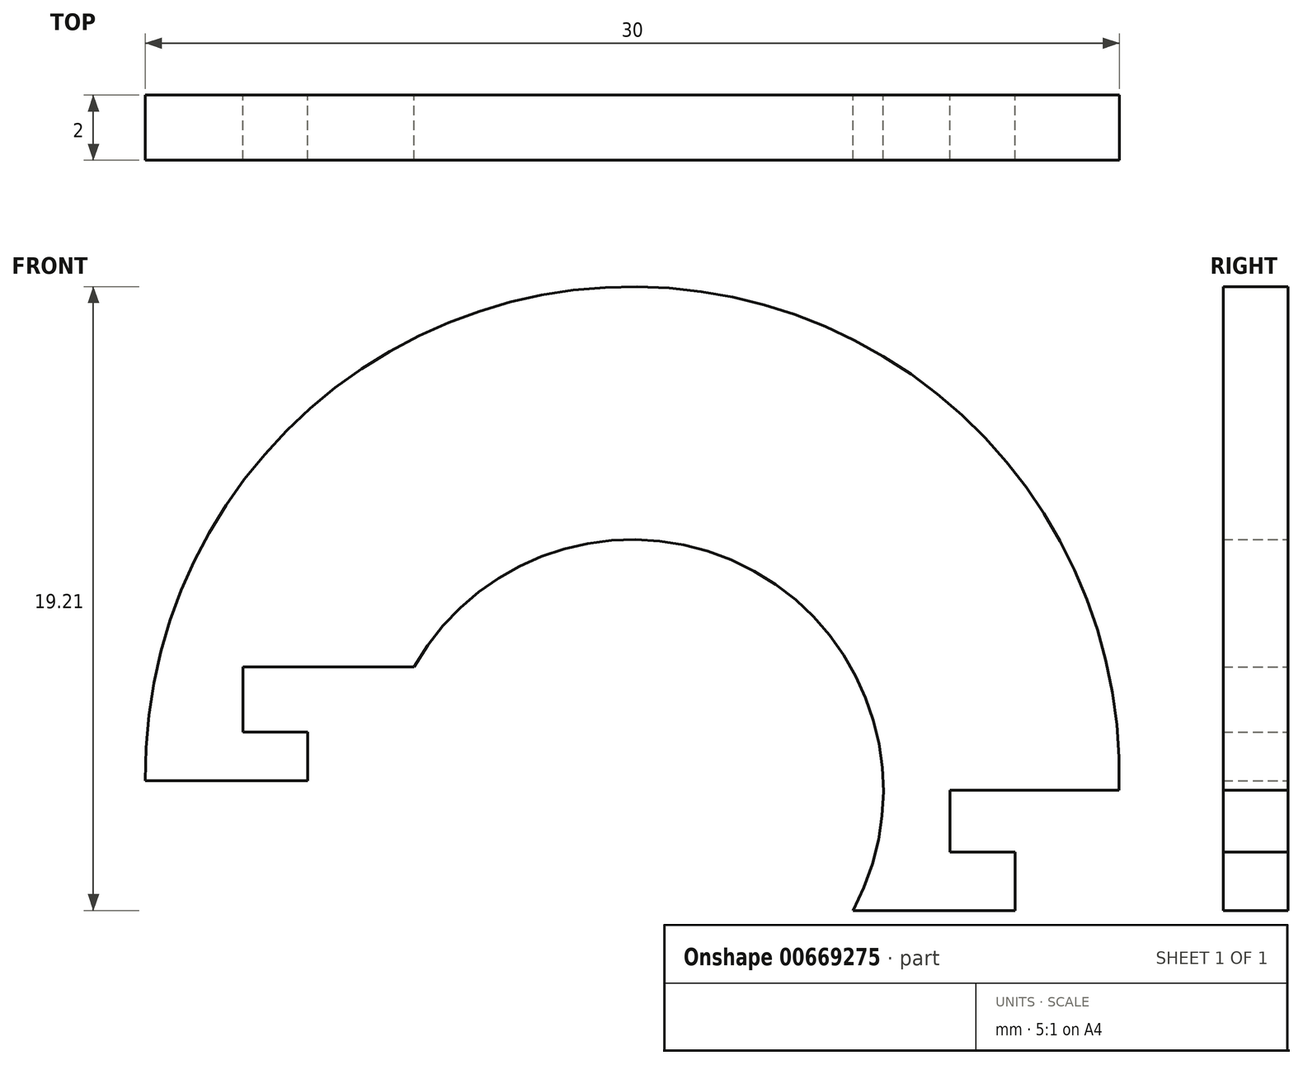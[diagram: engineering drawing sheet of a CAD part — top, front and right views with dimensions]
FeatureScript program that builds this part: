
annotation { "Feature Type Name" : "Feature", "Feature Type Description" : "" }
export const myFeature = defineFeature(function(context is Context, id is Id, definition is map)
    precondition{}
    {
        {
            var Q0;
            Q0=qCreatedBy(makeId("Front.planeOp"),FACE);
            var sketch = newSketch(context, id + "F0", { "sketchPlane" : qUnion([Q0])});
            skLineSegment(sketch, "E0", {"start": v(-15, 0.3) * mm, "end": v(-10, 0.3) * mm});
            skLineSegment(sketch, "E1", {"start": v(-10, 0.3) * mm, "end": v(-10, 1.8) * mm});
            skLineSegment(sketch, "E2", {"start": v(-10, 1.8) * mm, "end": v(-12, 1.8) * mm});
            skLineSegment(sketch, "E3", {"start": v(-12, 1.8) * mm, "end": v(-12, 3.8) * mm});
            skLineSegment(sketch, "E4", {"start": v(-12, 3.8) * mm, "end": v(-6.74, 3.8) * mm});
            skLineSegment(sketch, "E5", {"start": v(14.98, 0) * mm, "end": v(9.78, 0) * mm});
            skLineSegment(sketch, "E6", {"start": v(9.78, 0) * mm, "end": v(9.78, -1.9) * mm});
            skLineSegment(sketch, "E7", {"start": v(9.78, -1.9) * mm, "end": v(11.78, -1.9) * mm});
            skLineSegment(sketch, "E8", {"start": v(11.78, -1.9) * mm, "end": v(11.78, -3.7) * mm});
            skLineSegment(sketch, "E9", {"start": v(11.78, -3.7) * mm, "end": v(6.78, -3.7) * mm});
            skLineSegment(sketch, "E10", {"start": v(-20.23, 0) * mm, "end": v(29.2, 0) * mm});
            skArc(sketch, "E11", {"start": v(14.98, 0) * mm, "mid": v(0.14, 15.51) * mm, "end": v(-15, 0.3) * mm});
            skArc(sketch, "E12", {"start": v(6.78, -3.7) * mm, "mid": v(3.74, 6.75) * mm, "end": v(-6.74, 3.8) * mm});
            skSolve(sketch);
        }
        {
            var Q0;
            Q0=qSketchRegion(id+"F0",true);
            extrude(context, id + "F1", {"entities" : qUnion([Q0]), "endBound" : BoundingType.SYMMETRIC, "depth" : 2 * mm, "offsetDistance" : 25 * mm});
        }
    });
